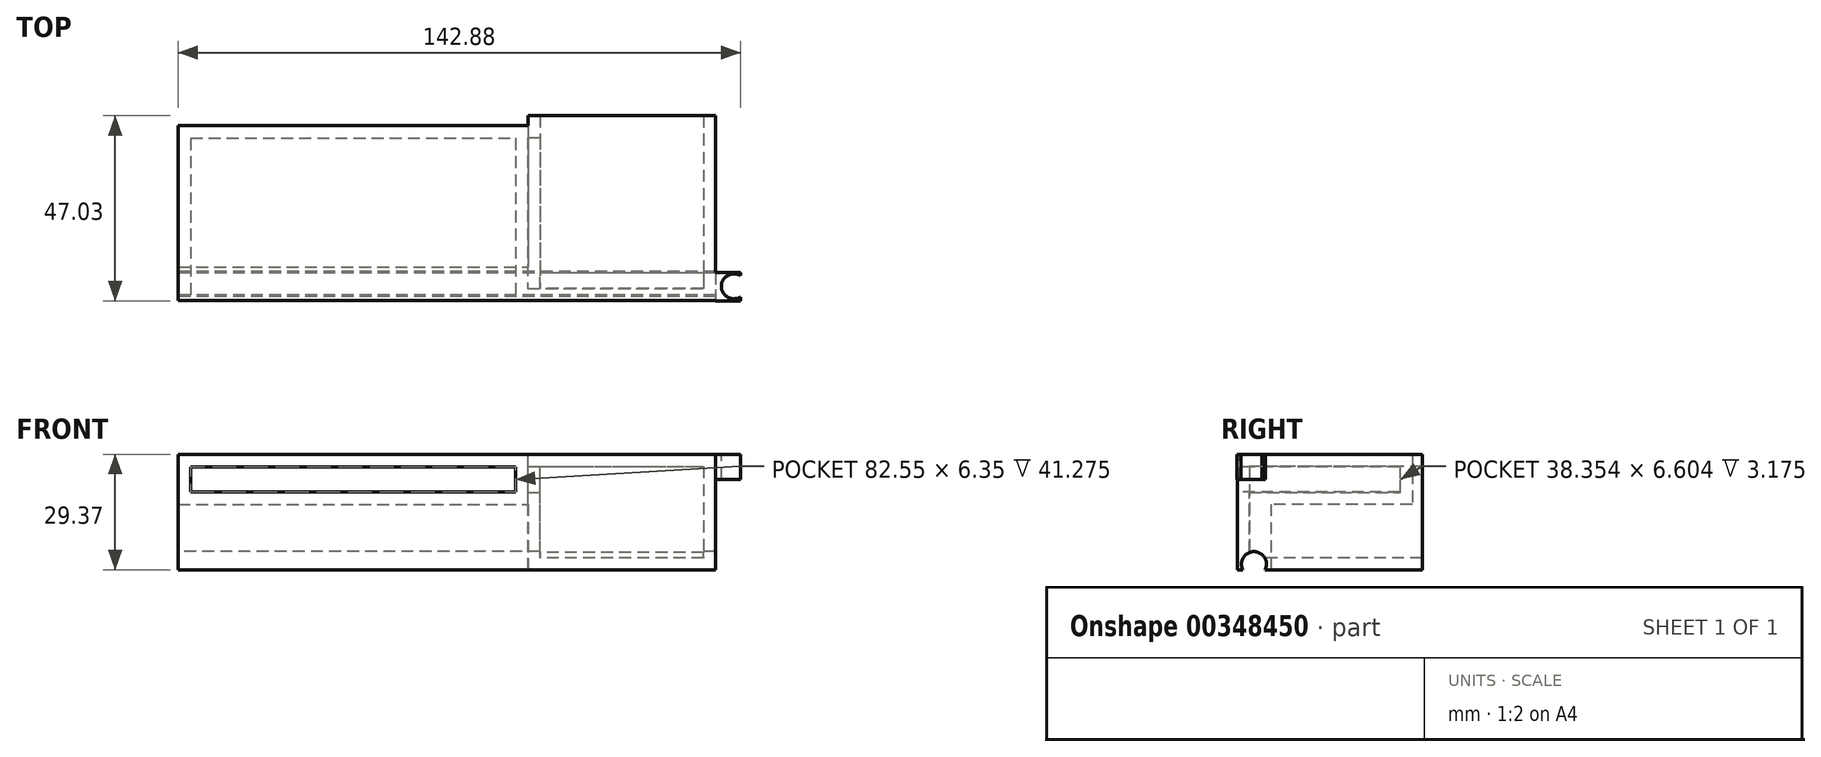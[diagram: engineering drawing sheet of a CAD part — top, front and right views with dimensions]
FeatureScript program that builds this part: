
annotation { "Feature Type Name" : "Feature", "Feature Type Description" : "" }
export const myFeature = defineFeature(function(context is Context, id is Id, definition is map)
    precondition{}
    {
        {
            var Q0;
            Q0=qCreatedBy(makeId("Top.planeOp"),FACE);
            var sketch = newSketch(context, id + "F0", { "sketchPlane" : qUnion([Q0])});
            skLineSegment(sketch, "E0.bottom", {"start": v(-49.95, 19.9) * mm, "end": v(32.6, 19.9) * mm});
            skLineSegment(sketch, "E0.top", {"start": v(-49.95, -18.2) * mm, "end": v(32.6, -18.2) * mm});
            skLineSegment(sketch, "E0.left", {"start": v(-49.95, 19.9) * mm, "end": v(-49.95, -18.2) * mm});
            skLineSegment(sketch, "E0.right", {"start": v(32.6, 19.9) * mm, "end": v(32.6, -18.2) * mm});
            skSolve(sketch);
        }
        {
            var Q0;
            Q0=makeQuery(id+"F0.imprint","IMPRINT",FACE,{"disambiguationData":[TD([[makeQuery(id+"F0.imprint","IMPRINT",EDGE,{"derivedFrom":sQuery(id+"F0.wireOp",EDGE,"E0.bottom")}),-1.0]])]});
            extrude(context, id + "F1", {"entities" : qUnion([Q0]), "depth" : 6.35 * mm});
        }
        {
            var Q0;
            Q0=makeQuery(id+"F1.opExtrude","CAP_FACE",FACE,{"disambiguationData":[OSD([sQuery(id+"F0.wireOp",EDGE,"E0.bottom"),sQuery(id+"F0.wireOp",EDGE,"E0.top"),sQuery(id+"F0.wireOp",EDGE,"E0.left"),sQuery(id+"F0.wireOp",EDGE,"E0.right")])],"isStart":false});
            extrude(context, id + "F2", {"entities" : qUnion([Q0]), "operationType" : NewBodyOperationType.ADD, "depth" : 3.17 * mm});
        }
        {
            var Q0;
            Q0=makeQuery(id+"F1.opExtrude","CAP_FACE",FACE,{"disambiguationData":[OSD([sQuery(id+"F0.wireOp",EDGE,"E0.bottom"),sQuery(id+"F0.wireOp",EDGE,"E0.top"),sQuery(id+"F0.wireOp",EDGE,"E0.left"),sQuery(id+"F0.wireOp",EDGE,"E0.right")])],"isStart":true});
            extrude(context, id + "F3", {"entities" : qUnion([Q0]), "operationType" : NewBodyOperationType.ADD, "depth" : 3.17 * mm});
        }
        {
            var Q0;
            {var subQ0=sQuery(id+"F0.wireOp",EDGE,"E0.top");Q0=makeQuery(id+"F3.boolean.opBoolean","MERGE",FACE,{"derivedFrom":[makeQuery(id+"F2.boolean.opBoolean","MERGE",FACE,{"derivedFrom":[makeQuery(id+"F1.opExtrude","SWEPT_FACE",FACE,{"disambiguationData":[OSD([subQ0])]}),makeQuery(id+"F2.opExtrude","SWEPT_FACE",FACE,{"disambiguationData":[OSD([subQ0])]})]}),makeQuery(id+"F3.opExtrude","SWEPT_FACE",FACE,{"disambiguationData":[OSD([subQ0])]})]});}
            extrude(context, id + "F4", {"entities" : qUnion([Q0]), "operationType" : NewBodyOperationType.ADD, "depth" : 3.17 * mm});
        }
        {
            var Q0;
            {var subQ0=sQuery(id+"F0.wireOp",EDGE,"E0.left");Q0=makeQuery(id+"F4.boolean.opBoolean","MERGE",FACE,{"derivedFrom":[makeQuery(id+"F3.boolean.opBoolean","MERGE",FACE,{"derivedFrom":[makeQuery(id+"F2.boolean.opBoolean","MERGE",FACE,{"derivedFrom":[makeQuery(id+"F1.opExtrude","SWEPT_FACE",FACE,{"disambiguationData":[OSD([subQ0])]}),makeQuery(id+"F2.opExtrude","SWEPT_FACE",FACE,{"disambiguationData":[OSD([subQ0])]})]}),makeQuery(id+"F3.opExtrude","SWEPT_FACE",FACE,{"disambiguationData":[OSD([subQ0])]})]}),makeQuery(id+"F4.opExtrude","SWEPT_FACE",FACE,{"disambiguationData":[OSD([sQuery(id+"F0.wireOp",EDGE,"E0.top"),subQ0])]})]});}
            extrude(context, id + "F5", {"entities" : qUnion([Q0]), "operationType" : NewBodyOperationType.ADD, "depth" : 3.17 * mm});
        }
        {
            var Q0;
            {var subQ0=sQuery(id+"F0.wireOp",EDGE,"E0.right");Q0=makeQuery(id+"F4.boolean.opBoolean","MERGE",FACE,{"derivedFrom":[makeQuery(id+"F3.boolean.opBoolean","MERGE",FACE,{"derivedFrom":[makeQuery(id+"F2.boolean.opBoolean","MERGE",FACE,{"derivedFrom":[makeQuery(id+"F1.opExtrude","SWEPT_FACE",FACE,{"disambiguationData":[OSD([subQ0])]}),makeQuery(id+"F2.opExtrude","SWEPT_FACE",FACE,{"disambiguationData":[OSD([subQ0])]})]}),makeQuery(id+"F3.opExtrude","SWEPT_FACE",FACE,{"disambiguationData":[OSD([subQ0])]})]}),makeQuery(id+"F4.opExtrude","SWEPT_FACE",FACE,{"disambiguationData":[OSD([sQuery(id+"F0.wireOp",EDGE,"E0.top"),subQ0])]})]});}
            extrude(context, id + "F6", {"entities" : qUnion([Q0]), "operationType" : NewBodyOperationType.ADD, "depth" : 3.17 * mm});
        }
        {
            var Q0;
            {var subQ0=sQuery(id+"F0.wireOp",EDGE,"E0.bottom");Q0=makeQuery(id+"F6.boolean.opBoolean","MERGE",FACE,{"derivedFrom":[makeQuery(id+"F5.boolean.opBoolean","MERGE",FACE,{"derivedFrom":[makeQuery(id+"F3.boolean.opBoolean","MERGE",FACE,{"derivedFrom":[makeQuery(id+"F2.boolean.opBoolean","MERGE",FACE,{"derivedFrom":[makeQuery(id+"F1.opExtrude","SWEPT_FACE",FACE,{"disambiguationData":[OSD([subQ0])]}),makeQuery(id+"F2.opExtrude","SWEPT_FACE",FACE,{"disambiguationData":[OSD([subQ0])]})]}),makeQuery(id+"F3.opExtrude","SWEPT_FACE",FACE,{"disambiguationData":[OSD([subQ0])]})]}),makeQuery(id+"F5.opExtrude","SWEPT_FACE",FACE,{"disambiguationData":[OSD([subQ0,sQuery(id+"F0.wireOp",EDGE,"E0.left")])]})]}),makeQuery(id+"F6.opExtrude","SWEPT_FACE",FACE,{"disambiguationData":[OSD([subQ0,sQuery(id+"F0.wireOp",EDGE,"E0.right")])]})]});}
            extrude(context, id + "F7", {"entities" : qUnion([Q0]), "operationType" : NewBodyOperationType.ADD, "depth" : 3.17 * mm});
        }
        {
            var Q0;
            {var subQ0=sQuery(id+"F0.wireOp",EDGE,"E0.right");var subQ1=sQuery(id+"F0.wireOp",EDGE,"E0.top");var subQ2=sQuery(id+"F0.wireOp",EDGE,"E0.left");Q0=makeQuery(id+"F6.boolean.opBoolean","MERGE",FACE,{"derivedFrom":[makeQuery(id+"F5.boolean.opBoolean","MERGE",FACE,{"derivedFrom":[makeQuery(id+"F4.opExtrude","CAP_FACE",FACE,{"disambiguationData":[OSD([subQ1])],"isStart":false}),makeQuery(id+"F5.opExtrude","SWEPT_FACE",FACE,{"disambiguationData":[OSD([subQ1,subQ2]),TDD([makeQuery(id+"F4.opExtrude","CAP_EDGE",EDGE,{"disambiguationData":[OSD([subQ1,subQ2])],"isStart":false})])]})]}),makeQuery(id+"F6.opExtrude","SWEPT_FACE",FACE,{"disambiguationData":[OSD([subQ1,subQ0]),TDD([makeQuery(id+"F4.opExtrude","CAP_EDGE",EDGE,{"disambiguationData":[OSD([subQ1,subQ0])],"isStart":false})])]})]});}
            var Q1;
            Q1=makeQuery(id+"F1.opExtrude","SWEPT_BODY",BODY,{"disambiguationData":[OSD([sQuery(id+"F0.wireOp",EDGE,"E0.bottom"),sQuery(id+"F0.wireOp",EDGE,"E0.top"),sQuery(id+"F0.wireOp",EDGE,"E0.left"),sQuery(id+"F0.wireOp",EDGE,"E0.right")])]});
            shell(context, id + "F8", {"entities" : qUnion([Q0]), "parts" : qUnion([Q1]), "thickness" : 3.17 * mm});
        }
        {
            var Q0;
            {var subQ0=sQuery(id+"F0.wireOp",EDGE,"E0.right");Q0=makeQuery(id+"F7.boolean.opBoolean","MERGE",FACE,{"derivedFrom":[makeQuery(id+"F6.opExtrude","CAP_FACE",FACE,{"disambiguationData":[OSD([sQuery(id+"F0.wireOp",EDGE,"E0.top"),subQ0])],"isStart":false}),makeQuery(id+"F7.opExtrude","SWEPT_FACE",FACE,{"disambiguationData":[OSD([sQuery(id+"F0.wireOp",EDGE,"E0.bottom"),subQ0])]})]});}
            extrude(context, id + "F9", {"entities" : qUnion([Q0]), "operationType" : NewBodyOperationType.ADD, "depth" : 47.62 * mm});
        }
        {
            var Q0;
            {var subQ0=sQuery(id+"F0.wireOp",EDGE,"E0.right");var subQ1=sQuery(id+"F0.wireOp",EDGE,"E0.bottom");var subQ2=makeQuery(id+"F3.opExtrude","CAP_VERTEX",VERTEX,{"disambiguationData":[OSD([subQ1,subQ0])],"isStart":false});var subQ3=sQuery(id+"F0.wireOp",EDGE,"E0.top");var subQ4=makeQuery(id+"F4.boolean.opBoolean","MERGE",EDGE,{"derivedFrom":[makeQuery(id+"F3.opExtrude","CAP_EDGE",EDGE,{"disambiguationData":[OSD([subQ0])],"isStart":false}),makeQuery(id+"F4.opExtrude","SWEPT_EDGE",EDGE,{"disambiguationData":[OSD([subQ3,subQ0]),TDD([makeQuery(id+"F3.opExtrude","CAP_VERTEX",VERTEX,{"disambiguationData":[OSD([subQ3,subQ0])],"isStart":false})])]})]});var subQ5=sQuery(id+"F0.wireOp",EDGE,"E0.left");Q0=makeQuery(id+"F9.boolean.opBoolean","MERGE",FACE,{"derivedFrom":[makeQuery(id+"F7.boolean.opBoolean","MERGE",FACE,{"derivedFrom":[makeQuery(id+"F6.boolean.opBoolean","MERGE",FACE,{"derivedFrom":[makeQuery(id+"F5.boolean.opBoolean","MERGE",FACE,{"derivedFrom":[makeQuery(id+"F4.boolean.opBoolean","MERGE",FACE,{"derivedFrom":[makeQuery(id+"F3.opExtrude","CAP_FACE",FACE,{"disambiguationData":[OSD([subQ1,subQ3,subQ5,subQ0])],"isStart":false}),makeQuery(id+"F4.opExtrude","SWEPT_FACE",FACE,{"disambiguationData":[OSD([subQ3]),TDD([makeQuery(id+"F3.opExtrude","CAP_EDGE",EDGE,{"disambiguationData":[OSD([subQ3])],"isStart":false})])]})]}),makeQuery(id+"F5.opExtrude","SWEPT_FACE",FACE,{"disambiguationData":[OSD([subQ3,subQ5]),TDD([makeQuery(id+"F4.boolean.opBoolean","MERGE",EDGE,{"derivedFrom":[makeQuery(id+"F3.opExtrude","CAP_EDGE",EDGE,{"disambiguationData":[OSD([subQ5])],"isStart":false}),makeQuery(id+"F4.opExtrude","SWEPT_EDGE",EDGE,{"disambiguationData":[OSD([subQ3,subQ5]),TDD([makeQuery(id+"F3.opExtrude","CAP_VERTEX",VERTEX,{"disambiguationData":[OSD([subQ3,subQ5])],"isStart":false})])]})]})])]})]}),makeQuery(id+"F6.opExtrude","SWEPT_FACE",FACE,{"disambiguationData":[OSD([subQ3,subQ0]),TDD([subQ4])]})]}),makeQuery(id+"F7.opExtrude","SWEPT_FACE",FACE,{"disambiguationData":[OSD([subQ1,subQ5,subQ0]),TDD([makeQuery(id+"F6.boolean.opBoolean","MERGE",EDGE,{"derivedFrom":[makeQuery(id+"F5.boolean.opBoolean","MERGE",EDGE,{"derivedFrom":[makeQuery(id+"F3.opExtrude","CAP_EDGE",EDGE,{"disambiguationData":[OSD([subQ1])],"isStart":false}),makeQuery(id+"F5.opExtrude","SWEPT_EDGE",EDGE,{"disambiguationData":[OSD([subQ1,subQ5]),TDD([makeQuery(id+"F3.opExtrude","CAP_VERTEX",VERTEX,{"disambiguationData":[OSD([subQ1,subQ5])],"isStart":false})])]})]}),makeQuery(id+"F6.opExtrude","SWEPT_EDGE",EDGE,{"disambiguationData":[OSD([subQ1,subQ0]),TDD([subQ2])]})]})])]})]}),makeQuery(id+"F9.opExtrude","SWEPT_FACE",FACE,{"disambiguationData":[OSD([subQ1,subQ3,subQ0]),TDD([makeQuery(id+"F7.boolean.opBoolean","MERGE",EDGE,{"derivedFrom":[makeQuery(id+"F6.opExtrude","CAP_EDGE",EDGE,{"disambiguationData":[OSD([subQ3,subQ0]),TDD([subQ4])],"isStart":false}),makeQuery(id+"F7.opExtrude","SWEPT_EDGE",EDGE,{"disambiguationData":[OSD([subQ1,subQ0]),TDD([makeQuery(id+"F6.opExtrude","CAP_VERTEX",VERTEX,{"disambiguationData":[OSD([subQ1,subQ0]),TDD([subQ2])],"isStart":false})])]})]})])]})]});}
            var sketch = newSketch(context, id + "F10", { "sketchPlane" : qUnion([Q0])});
            skLineSegment(sketch, "E1", {"start": v(83.4, -23.07) * mm, "end": v(35.77, -23.07) * mm});
            skLineSegment(sketch, "E2", {"start": v(35.77, -23.07) * mm, "end": v(35.77, 21.38) * mm});
            skLineSegment(sketch, "E3", {"start": v(35.77, 21.38) * mm, "end": v(83.4, 21.38) * mm});
            skLineSegment(sketch, "E4", {"start": v(83.4, -23.07) * mm, "end": v(83.4, 21.38) * mm});
            skSolve(sketch);
        }
        {
            var Q0;
            Q0=makeQuery(id+"F10.imprint","IMPRINT",FACE,{"disambiguationData":[TD([[makeQuery(id+"F10.imprint","IMPRINT",EDGE,{"derivedFrom":sQuery(id+"F10.wireOp",EDGE,"E1")}),1.0]])]});
            extrude(context, id + "F11", {"entities" : qUnion([Q0]), "operationType" : NewBodyOperationType.ADD, "depth" : 16.67 * mm});
        }
        {
            var Q0;
            {var subQ0=sQuery(id+"F0.wireOp",EDGE,"E0.right");var subQ1=sQuery(id+"F0.wireOp",EDGE,"E0.bottom");Q0=makeQuery(id+"F11.boolean.opBoolean","MERGE",FACE,{"derivedFrom":[makeQuery(id+"F9.boolean.opBoolean","MERGE",FACE,{"derivedFrom":[makeQuery(id+"F7.opExtrude","CAP_FACE",FACE,{"disambiguationData":[OSD([subQ1,sQuery(id+"F0.wireOp",EDGE,"E0.left"),subQ0])],"isStart":false}),makeQuery(id+"F9.opExtrude","SWEPT_FACE",FACE,{"disambiguationData":[OSD([subQ1,subQ0])]})]}),makeQuery(id+"F11.opExtrude","SWEPT_FACE",FACE,{"disambiguationData":[OSD([sQuery(id+"F10.wireOp",EDGE,"E1")])]})]});}
            var sketch = newSketch(context, id + "F12", { "sketchPlane" : qUnion([Q0])});
            skLineSegment(sketch, "E5", {"start": v(-35.77, -3.17) * mm, "end": v(-35.77, 9.53) * mm});
            skLineSegment(sketch, "E6", {"start": v(-35.77, 9.53) * mm, "end": v(-83.4, 9.53) * mm});
            skLineSegment(sketch, "E7", {"start": v(-83.4, 9.53) * mm, "end": v(-83.4, -19.84) * mm});
            skLineSegment(sketch, "E8", {"start": v(-83.4, -19.84) * mm, "end": v(-35.77, -19.84) * mm});
            skLineSegment(sketch, "E9", {"start": v(-35.77, -19.84) * mm, "end": v(-35.77, -3.18) * mm});
            skSolve(sketch);
        }
        {
            var Q0;
            Q0=makeQuery(id+"F12.imprint","IMPRINT",FACE,{"disambiguationData":[TD([[makeQuery(id+"F12.imprint","IMPRINT",EDGE,{"derivedFrom":sQuery(id+"F12.wireOp",EDGE,"E5")}),1.0]])]});
            extrude(context, id + "F13", {"entities" : qUnion([Q0]), "operationType" : NewBodyOperationType.ADD, "depth" : 2.54 * mm});
        }
        {
            var Q0;
            Q0=makeQuery(id+"F13.opExtrude","CAP_FACE",FACE,{"disambiguationData":[OSD([sQuery(id+"F12.wireOp",EDGE,"E5"),sQuery(id+"F12.wireOp",EDGE,"E6"),sQuery(id+"F12.wireOp",EDGE,"E7"),sQuery(id+"F12.wireOp",EDGE,"E8"),sQuery(id+"F12.wireOp",EDGE,"E9")])],"isStart":false});
            shell(context, id + "F14", {"entities" : qUnion([Q0]), "thickness" : 3.05 * mm});
        }
        {
            var Q0;
            Q0=makeQuery(id+"F13.boolean.opBoolean","MERGE",FACE,{"derivedFrom":[makeQuery(id+"F11.opExtrude","SWEPT_FACE",FACE,{"disambiguationData":[OSD([sQuery(id+"F10.wireOp",EDGE,"E2")])]}),makeQuery(id+"F13.opExtrude","SWEPT_FACE",FACE,{"disambiguationData":[OSD([sQuery(id+"F12.wireOp",EDGE,"E5"),sQuery(id+"F12.wireOp",EDGE,"E9")])]})]});
            var sketch = newSketch(context, id + "F15", { "sketchPlane" : qUnion([Q0])});
            skLineSegment(sketch, "E10", {"start": v(12.85, -3.18) * mm, "end": v(12.85, -19.84) * mm});
            skLineSegment(sketch, "E11", {"start": v(12.85, -19.84) * mm, "end": v(21.38, -19.84) * mm});
            skLineSegment(sketch, "E12", {"start": v(21.38, -19.84) * mm, "end": v(21.38, -3.18) * mm});
            skLineSegment(sketch, "E13", {"start": v(21.38, -3.18) * mm, "end": v(12.85, -3.18) * mm});
            skSolve(sketch);
        }
        {
            var Q0;
            Q0=makeQuery(id+"F15.imprint","IMPRINT",FACE,{"disambiguationData":[TD([[makeQuery(id+"F15.imprint","IMPRINT",EDGE,{"derivedFrom":sQuery(id+"F15.wireOp",EDGE,"E10")}),1.0]])]});
            extrude(context, id + "F16", {"entities" : qUnion([Q0]), "operationType" : NewBodyOperationType.ADD, "depth" : 88.9 * mm});
        }
        {
            var Q0;
            {var subQ0=sQuery(id+"F0.wireOp",EDGE,"E0.left");Q0=makeQuery(id+"F16.boolean.opBoolean","MERGE",FACE,{"derivedFrom":[makeQuery(id+"F7.boolean.opBoolean","MERGE",FACE,{"derivedFrom":[makeQuery(id+"F5.opExtrude","CAP_FACE",FACE,{"disambiguationData":[OSD([sQuery(id+"F0.wireOp",EDGE,"E0.top"),subQ0])],"isStart":false}),makeQuery(id+"F7.opExtrude","SWEPT_FACE",FACE,{"disambiguationData":[OSD([sQuery(id+"F0.wireOp",EDGE,"E0.bottom"),subQ0])]})]}),makeQuery(id+"F16.opExtrude","CAP_FACE",FACE,{"disambiguationData":[OSD([sQuery(id+"F15.wireOp",EDGE,"E10"),sQuery(id+"F15.wireOp",EDGE,"E11"),sQuery(id+"F15.wireOp",EDGE,"E12"),sQuery(id+"F15.wireOp",EDGE,"E13")])],"isStart":false})]});}
            var sketch = newSketch(context, id + "F17", { "sketchPlane" : qUnion([Q0])});
            skLineSegment(sketch, "E14", {"start": v(12.85, -3.17) * mm, "end": v(21.38, -3.17) * mm});
            skLineSegment(sketch, "E15", {"start": v(21.38, -3.17) * mm, "end": v(21.38, -19.84) * mm});
            skLineSegment(sketch, "E16", {"start": v(21.38, -19.84) * mm, "end": v(12.85, -19.84) * mm});
            skLineSegment(sketch, "E17", {"start": v(12.85, -19.84) * mm, "end": v(12.85, -3.18) * mm});
            skSolve(sketch);
        }
        {
            var Q0;
            Q0=makeQuery(id+"F17.imprint","IMPRINT",FACE,{"disambiguationData":[TD([[makeQuery(id+"F17.imprint","IMPRINT",EDGE,{"derivedFrom":sQuery(id+"F17.wireOp",EDGE,"E14")}),-1.0]])]});
            var sketch = newSketch(context, id + "F18", { "sketchPlane" : qUnion([Q0])});
            skCircle(sketch, "E18", {"center": v(17.14, -18.38) * mm, "radius": 1.59 * mm});
            skSolve(sketch);
        }
        {
            var Q0;
            Q0=sQuery(id+"F18.wireOp",VERTEX,"E18.center");
            var Q1;
            Q1=makeQuery(id+"F1.opExtrude","SWEPT_BODY",BODY,{"disambiguationData":[OSD([sQuery(id+"F0.wireOp",EDGE,"E0.bottom"),sQuery(id+"F0.wireOp",EDGE,"E0.top"),sQuery(id+"F0.wireOp",EDGE,"E0.left"),sQuery(id+"F0.wireOp",EDGE,"E0.right")])]});
            hole(context, id + "F19", {"style" : HoleStyle.SIMPLE, "endStyle" : HoleEndStyle.THROUGH, "holeDiameter" : 6.35 * mm, "isTappedThrough" : true, "tappedDepth" : 12.7 * mm, "tapClearance" : 3, "locations" : qUnion([Q0]), "scope" : qUnion([Q1])});
        }
        {
            var Q0;
            Q0=makeQuery(id+"F13.boolean.opBoolean","MERGE",FACE,{"derivedFrom":[makeQuery(id+"F11.boolean.opBoolean","MERGE",FACE,{"derivedFrom":[makeQuery(id+"F9.opExtrude","CAP_FACE",FACE,{"disambiguationData":[OSD([sQuery(id+"F0.wireOp",EDGE,"E0.bottom"),sQuery(id+"F0.wireOp",EDGE,"E0.top"),sQuery(id+"F0.wireOp",EDGE,"E0.right")])],"isStart":false}),makeQuery(id+"F11.opExtrude","SWEPT_FACE",FACE,{"disambiguationData":[OSD([sQuery(id+"F10.wireOp",EDGE,"E4")])]})]}),makeQuery(id+"F13.opExtrude","SWEPT_FACE",FACE,{"disambiguationData":[OSD([sQuery(id+"F12.wireOp",EDGE,"E7")])]})]});
            var sketch = newSketch(context, id + "F20", { "sketchPlane" : qUnion([Q0])});
            skLineSegment(sketch, "E19", {"start": v(-17.14, -15.2) * mm, "end": v(-17.14, 9.52) * mm});
            skSolve(sketch);
        }
        {
            var Q0;
            {var subQ7=sQuery(id+"F20.wireOp",EDGE,"E19");Q0=makeQuery(id+"F20.imprint","IMPRINT",FACE,{"disambiguationData":[TD([[makeQuery(id+"F20.imprint","IMPRINT",EDGE,{"derivedFrom":subQ7}),-1.0]])]});}
            var sketch = newSketch(context, id + "F21", { "sketchPlane" : qUnion([Q0])});
            skLineSegment(sketch, "E20.bottom", {"start": v(-14.28, 9.52) * mm, "end": v(-21.42, 9.52) * mm});
            skLineSegment(sketch, "E20.top", {"start": v(-14.28, 3.17) * mm, "end": v(-21.42, 3.17) * mm});
            skLineSegment(sketch, "E20.left", {"start": v(-14.28, 9.52) * mm, "end": v(-14.28, 3.17) * mm});
            skLineSegment(sketch, "E20.right", {"start": v(-21.42, 9.52) * mm, "end": v(-21.42, 3.17) * mm});
            skSolve(sketch);
        }
        {
            var Q0;
            Q0 = qSketchRegion(id + "F21", true);
            extrude(context, id + "F22", {"entities" : qUnion([Q0]), "operationType" : NewBodyOperationType.ADD, "depth" : 6.35 * mm});
        }
        {
            var Q0;
            Q0=makeQuery(id+"F22.opExtrude","SWEPT_FACE",FACE,{"disambiguationData":[OSD([sQuery(id+"F21.wireOp",EDGE,"E20.bottom")])]});
            var sketch = newSketch(context, id + "F23", { "sketchPlane" : qUnion([Q0])});
            skCircle(sketch, "E21", {"center": v(88.06, -17.75) * mm, "radius": 1.6 * mm});
            skSolve(sketch);
        }
        {
            var Q0;
            Q0=sQuery(id+"F23.wireOp",VERTEX,"E21.center");
            var Q1;
            Q1=makeQuery(id+"F1.opExtrude","SWEPT_BODY",BODY,{"disambiguationData":[OSD([sQuery(id+"F0.wireOp",EDGE,"E0.bottom"),sQuery(id+"F0.wireOp",EDGE,"E0.top"),sQuery(id+"F0.wireOp",EDGE,"E0.left"),sQuery(id+"F0.wireOp",EDGE,"E0.right")])]});
            hole(context, id + "F24", {"style" : HoleStyle.SIMPLE, "endStyle" : HoleEndStyle.THROUGH, "holeDiameter" : 6.35 * mm, "isTappedThrough" : true, "tappedDepth" : 12.7 * mm, "tapClearance" : 3, "locations" : qUnion([Q0]), "scope" : qUnion([Q1])});
        }
    });
